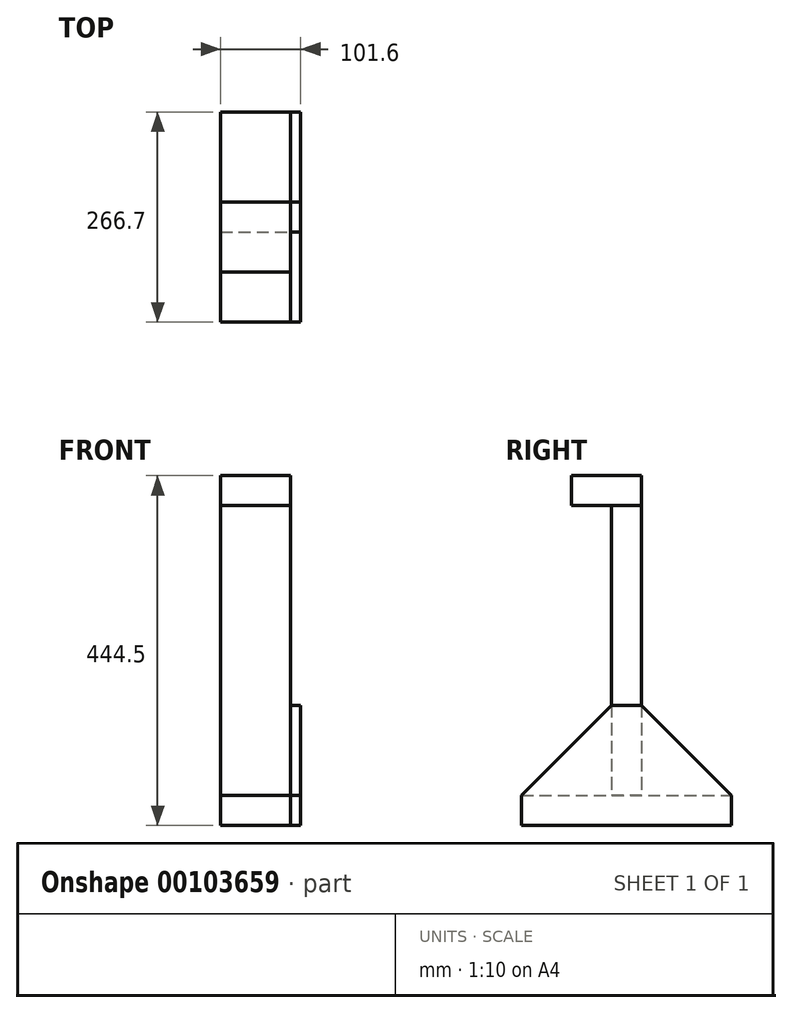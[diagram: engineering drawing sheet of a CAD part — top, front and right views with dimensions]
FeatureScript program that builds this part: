
annotation { "Feature Type Name" : "Feature", "Feature Type Description" : "" }
export const myFeature = defineFeature(function(context is Context, id is Id, definition is map)
    precondition{}
    {
        {
            var Q0;
            Q0=qCreatedBy(makeId("Top.planeOp"),FACE);
            var sketch = newSketch(context, id + "F0", { "sketchPlane" : qUnion([Q0])});
            skLineSegment(sketch, "E0.bottom", {"start": v(0, 0) * mm, "end": v(88.9, 0) * mm});
            skLineSegment(sketch, "E0.top", {"start": v(0, -38.1) * mm, "end": v(88.9, -38.1) * mm});
            skLineSegment(sketch, "E0.left", {"start": v(0, 0) * mm, "end": v(0, -38.1) * mm});
            skLineSegment(sketch, "E0.right", {"start": v(88.9, 0) * mm, "end": v(88.9, -38.1) * mm});
            skSolve(sketch);
        }
        {
            var Q0;
            Q0 = qSketchRegion(id + "F0", true);
            extrude(context, id + "F1", {"entities" : qUnion([Q0]), "depth" : 368.3 * mm});
        }
        {
            var Q0;
            Q0=makeQuery(id+"F1.opExtrude","CAP_FACE",FACE,{"disambiguationData":[OSD([sQuery(id+"F0.wireOp",EDGE,"E0.bottom"),sQuery(id+"F0.wireOp",EDGE,"E0.top"),sQuery(id+"F0.wireOp",EDGE,"E0.left"),sQuery(id+"F0.wireOp",EDGE,"E0.right")])],"isStart":false});
            var sketch = newSketch(context, id + "F2", { "sketchPlane" : qUnion([Q0])});
            skPoint(sketch, "E1.0", {"position": v(88.9, 0) * mm});
            skLineSegment(sketch, "E2.0", {"start": v(0, 0) * mm, "end": v(0, -38.1) * mm});
            skLineSegment(sketch, "E3.0", {"start": v(0, -38.1) * mm, "end": v(88.9, -38.1) * mm});
            skLineSegment(sketch, "E4.bottom", {"start": v(88.9, 0) * mm, "end": v(0, 0) * mm});
            skLineSegment(sketch, "E4.top", {"start": v(88.9, -88.9) * mm, "end": v(0, -88.9) * mm});
            skLineSegment(sketch, "E4.left", {"start": v(88.9, 0) * mm, "end": v(88.9, -88.9) * mm});
            skLineSegment(sketch, "E4.right", {"start": v(0, 0) * mm, "end": v(0, -88.9) * mm});
            skSolve(sketch);
        }
        {
            var Q0;
            Q0 = qSketchRegion(id + "F2", true);
            extrude(context, id + "F3", {"entities" : qUnion([Q0]), "depth" : 38.1 * mm});
        }
        {
            var Q0;
            Q0=qCreatedBy(makeId("Front.planeOp"),FACE);
            var sketch = newSketch(context, id + "F4", { "sketchPlane" : qUnion([Q0])});
            skLineSegment(sketch, "E5.bottom", {"start": v(0, 0) * mm, "end": v(88.9, 0) * mm});
            skLineSegment(sketch, "E5.top", {"start": v(0, -38.1) * mm, "end": v(88.9, -38.1) * mm});
            skLineSegment(sketch, "E5.left", {"start": v(0, 0) * mm, "end": v(0, -38.1) * mm});
            skLineSegment(sketch, "E5.right", {"start": v(88.9, 0) * mm, "end": v(88.9, -38.1) * mm});
            skSolve(sketch);
        }
        {
            var Q0;
            Q0 = qSketchRegion(id + "F4", true);
            extrude(context, id + "F5", {"entities" : qUnion([Q0]), "depth" : 152.4 * mm, "hasSecondDirection" : true, "secondDirectionOppositeDirection" : true, "secondDirectionDepth" : 114.3 * mm});
        }
        {
            var Q0;
            Q0=makeQuery(id+"F5.opExtrude","SWEPT_FACE",FACE,{"disambiguationData":[OSD([sQuery(id+"F4.wireOp",EDGE,"E5.right")])]});
            var sketch = newSketch(context, id + "F6", { "sketchPlane" : qUnion([Q0])});
            skLineSegment(sketch, "E6", {"start": v(-152.4, -38.1) * mm, "end": v(-152.4, 0) * mm});
            skLineSegment(sketch, "E7", {"start": v(-152.4, 0) * mm, "end": v(-38.1, 114.3) * mm});
            skLineSegment(sketch, "E8", {"start": v(-38.1, 114.3) * mm, "end": v(0, 114.3) * mm});
            skLineSegment(sketch, "E9", {"start": v(0, 114.3) * mm, "end": v(114.3, 0) * mm});
            skLineSegment(sketch, "E10", {"start": v(114.3, 0) * mm, "end": v(114.3, -38.1) * mm});
            skLineSegment(sketch, "E11", {"start": v(114.3, -38.1) * mm, "end": v(-152.4, -38.1) * mm});
            skSolve(sketch);
        }
        {
            var Q0;
            Q0 = qSketchRegion(id + "F6", true);
            extrude(context, id + "F7", {"entities" : qUnion([Q0]), "depth" : 12.7 * mm});
        }
    });
